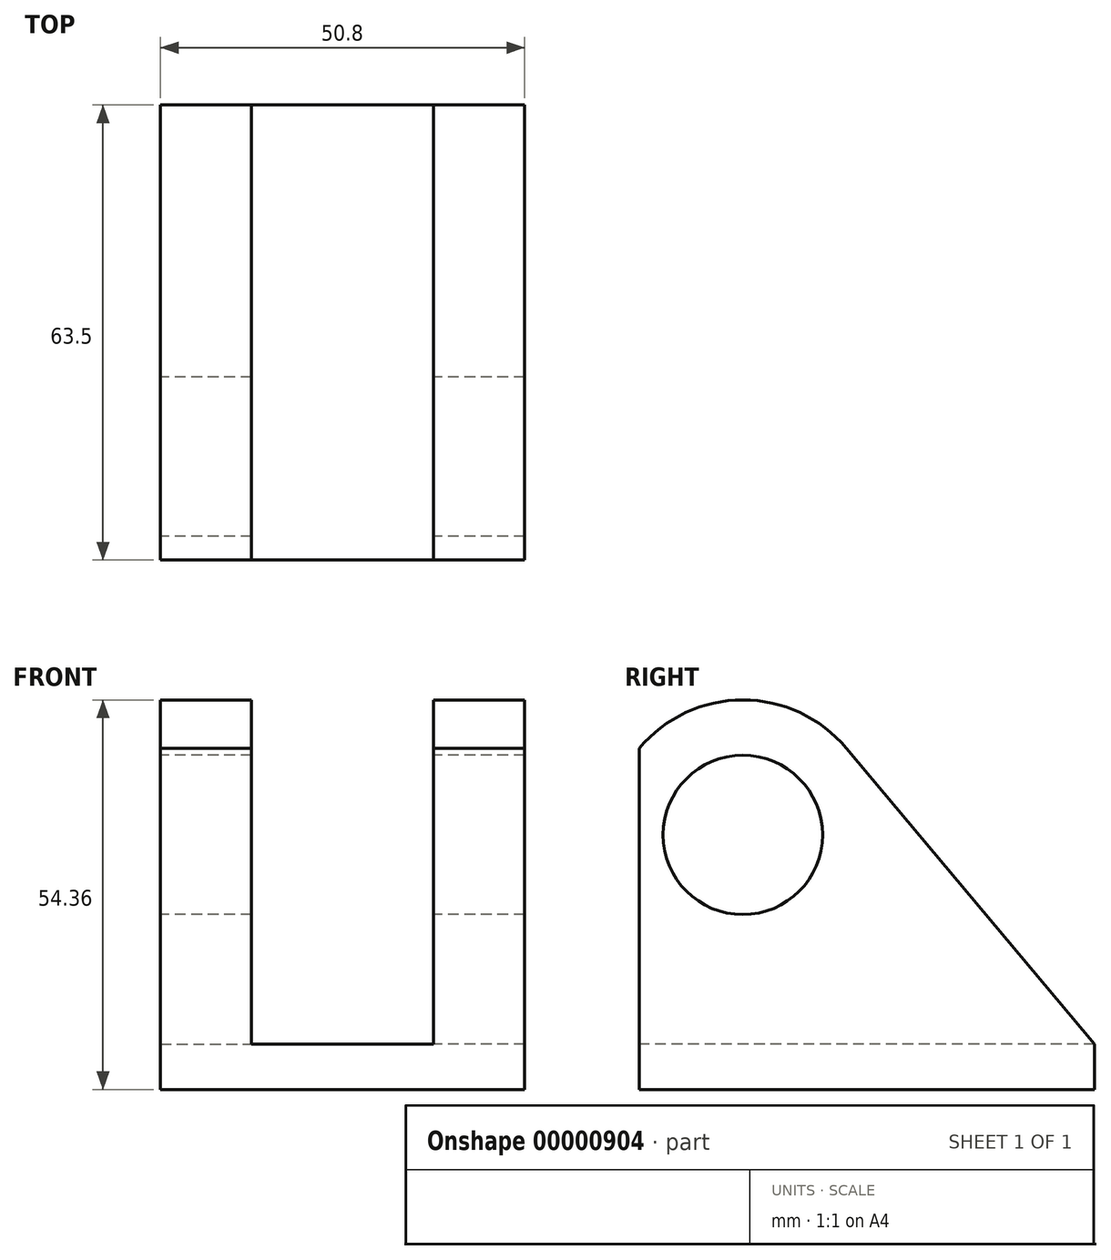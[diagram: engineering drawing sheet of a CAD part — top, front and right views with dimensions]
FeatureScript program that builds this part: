
annotation { "Feature Type Name" : "Feature", "Feature Type Description" : "" }
export const myFeature = defineFeature(function(context is Context, id is Id, definition is map)
    precondition{}
    {
        {
            var Q0;
            Q0=qCreatedBy(makeId("Right.planeOp"),FACE);
            var sketch = newSketch(context, id + "F0", { "sketchPlane" : qUnion([Q0])});
            skLineSegment(sketch, "E0", {"start": v(0, 0) * mm, "end": v(0, 41.28) * mm});
            skLineSegment(sketch, "E1", {"start": v(0, 41.28) * mm, "end": v(28.87, 41.28) * mm, "construction": true});
            skLineSegment(sketch, "E2", {"start": v(28.87, 41.28) * mm, "end": v(63.5, 0) * mm});
            skLineSegment(sketch, "E3", {"start": v(63.5, 0) * mm, "end": v(0, 0) * mm});
            skArc(sketch, "E4", {"start": v(28.87, 41.28) * mm, "mid": v(14.43, 48) * mm, "end": v(0, 41.28) * mm});
            skSolve(sketch);
        }
        {
            var Q0;
            Q0=makeQuery(id+"F0.imprint","IMPRINT",FACE,{"disambiguationData":[TD([[makeQuery(id+"F0.imprint","IMPRINT",EDGE,{"derivedFrom":sQuery(id+"F0.wireOp",EDGE,"E0")}),-1.0]])]});
            extrude(context, id + "F1", {"entities" : qUnion([Q0]), "depth" : 12.7 * mm});
        }
        {
            var Q0;
            Q0=makeQuery(id+"F1.opExtrude","SWEPT_FACE",FACE,{"disambiguationData":[OSD([sQuery(id+"F0.wireOp",EDGE,"E3")])]});
            var sketch = newSketch(context, id + "F2", { "sketchPlane" : qUnion([Q0])});
            skLineSegment(sketch, "E5.0", {"start": v(12.7, -63.5) * mm, "end": v(12.7, 0) * mm});
            skLineSegment(sketch, "E6.0", {"start": v(12.7, -63.5) * mm, "end": v(-38.1, -63.5) * mm});
            skLineSegment(sketch, "E7.0", {"start": v(12.7, 0) * mm, "end": v(-38.1, 0) * mm});
            skPoint(sketch, "E8.orphan", {"position": v(0, -63.5) * mm});
            skPoint(sketch, "E9.orphan", {"position": v(0, 0) * mm});
            skLineSegment(sketch, "E10", {"start": v(-38.1, 0) * mm, "end": v(-38.1, -63.5) * mm});
            skSolve(sketch);
        }
        {
            var Q0;
            {var subQ1=sQuery(id+"F2.wireOp",EDGE,"E10");Q0=makeQuery(id+"F2.imprint","IMPRINT",FACE,{"disambiguationData":[TD([[makeQuery(id+"F2.imprint","IMPRINT",EDGE,{"derivedFrom":subQ1}),1.0]])]});}
            var Q1;
            {var subQ1=sQuery(id+"F2.wireOp",EDGE,"E5.0");Q1=makeQuery(id+"F2.imprint","IMPRINT",FACE,{"disambiguationData":[TD([[makeQuery(id+"F2.imprint","IMPRINT",EDGE,{"derivedFrom":subQ1}),1.0]])]});}
            extrude(context, id + "F3", {"entities" : qUnion([Q0, Q1]), "operationType" : NewBodyOperationType.ADD, "depth" : 6.35 * mm});
        }
        {
            var Q0;
            Q0=makeQuery(id+"F3.opExtrude","CAP_EDGE",EDGE,{"disambiguationData":[OSD([sQuery(id+"F2.wireOp",EDGE,"E6.0")])],"isStart":false});
            cPlane(context, id + "F4", {"entities" : qUnion([Q0]), "cplaneType" : CPlaneType.MID_PLANE, "offset" : 152.4 * mm, "width" : 152.4 * mm, "height" : 152.4 * mm});
        }
        {
            var Q0;
            Q0=makeQuery(id+"F1.opExtrude","SWEPT_BODY",BODY,{"disambiguationData":[OSD([sQuery(id+"F0.wireOp",EDGE,"E0"),sQuery(id+"F0.wireOp",EDGE,"E2"),sQuery(id+"F0.wireOp",EDGE,"E3"),sQuery(id+"F0.wireOp",EDGE,"E4")])]});
            var Q1;
            Q1=qCreatedBy(id+"F4.planeOp",FACE);
            mirror(context, id + "F5", {"entities" : qUnion([Q0]), "mirrorPlane" : qUnion([Q1])});
        }
        {
            var Q0;
            Q0=makeQuery(id+"F1.opExtrude","SWEPT_BODY",BODY,{"disambiguationData":[OSD([sQuery(id+"F0.wireOp",EDGE,"E0"),sQuery(id+"F0.wireOp",EDGE,"E2"),sQuery(id+"F0.wireOp",EDGE,"E3"),sQuery(id+"F0.wireOp",EDGE,"E4")])]});
            var Q1;
            Q1=makeQuery(id+"F5.opPattern","COPY",BODY,{"derivedFrom":makeQuery(id+"F1.opExtrude","SWEPT_BODY",BODY,{"disambiguationData":[OSD([sQuery(id+"F0.wireOp",EDGE,"E0"),sQuery(id+"F0.wireOp",EDGE,"E2"),sQuery(id+"F0.wireOp",EDGE,"E3"),sQuery(id+"F0.wireOp",EDGE,"E4")])]}),"instanceName":"1"});
            booleanBodies(context, id + "F6", {"operationType" : BooleanOperationType.UNION, "tools" : qUnion([Q0, Q1])});
        }
        {
            var Q0;
            Q0=makeQuery(id+"F6.opBoolean","MERGE",FACE,{"derivedFrom":[makeQuery(id+"F3.opExtrude","SWEPT_FACE",FACE,{"disambiguationData":[OSD([sQuery(id+"F2.wireOp",EDGE,"E10")])]}),makeQuery(id+"F5.opPattern","COPY",FACE,{"derivedFrom":makeQuery(id+"F3.boolean.opBoolean","MERGE",FACE,{"derivedFrom":[makeQuery(id+"F1.opExtrude","CAP_FACE",FACE,{"disambiguationData":[OSD([sQuery(id+"F0.wireOp",EDGE,"E0"),sQuery(id+"F0.wireOp",EDGE,"E2"),sQuery(id+"F0.wireOp",EDGE,"E3"),sQuery(id+"F0.wireOp",EDGE,"E4")])],"isStart":false}),makeQuery(id+"F3.opExtrude","SWEPT_FACE",FACE,{"disambiguationData":[OSD([sQuery(id+"F2.wireOp",EDGE,"E5.0")])]})]}),"instanceName":"1"})]});
            var sketch = newSketch(context, id + "F7", { "sketchPlane" : qUnion([Q0])});
            skCircle(sketch, "E11", {"center": v(-14.43, 29.16) * mm, "radius": 11.11 * mm});
            skSolve(sketch);
        }
        {
            var Q0;
            Q0=makeQuery(id+"F7.imprint","IMPRINT",FACE,{"disambiguationData":[TD([[makeQuery(id+"F7.imprint","IMPRINT",EDGE,{"derivedFrom":sQuery(id+"F7.wireOp",EDGE,"E11")}),1.0]])]});
            extrude(context, id + "F8", {"entities" : qUnion([Q0]), "operationType" : NewBodyOperationType.REMOVE, "endBound" : BoundingType.THROUGH_ALL, "oppositeDirection" : true, "depth" : 25.4 * mm});
        }
        {
            var Q0;
            Q0=qCreatedBy(id+"F4.planeOp",FACE);
            var sketch = newSketch(context, id + "F9", { "sketchPlane" : qUnion([Q0])});
            skPoint(sketch, "E12", {"position": v(-14.43, 29.16) * mm});
            skSolve(sketch);
        }
    });
